# Revit family: Solarstone - Solarpanels
name_source: partatom
category: Generic Models
revit_build: Autodesk Revit 2018 (Build: 20170223_1515(x64)
units: mm (PartAtom-declared; Revit-internal decimal feet)

## family parameters
Always vertical = No
Can host rebar = No
Cut with Voids When Loaded = Yes
OmniClass Number = 23.80.00.00
OmniClass Title = Electric Power and Lighting
Part Type = Normal
Room Calculation Point = No
Round Connector Dimension = Use Diameter
Shared = No
Work Plane-Based = Yes

## types (2) — shared parameters
Aluminium Framing = SolarStone® - Aluminium, Painted
Default Panel Overlap = 43 mm
Developer = TULITEC
Developer URL = http://tulitec.com
Finishing Profile = SolarStone® - Finishing Profile
Fixing Plate = SolarStone® - Fixing Plate
Fuse Rating = 0 A
IFCExportAS = IfcDiscreteAccessoryType
Manufacturer = Solarstone
Manufacturer URL = https://solarstone.ee
Max Panel Vertical Overlap = 130 mm
Max Solar Panel Height = 2400 mm
Max Solar Panel Width = 2400 mm
Maximum Power Current (Imp) = 0 A
Maximum Power Rating (Pmax) = 0 VA
Maximum Power Voltage (Vmp) = 0 V
Maximum System Voltage = 0 V
Min Solar Panel Height = 900 mm
Min Solar Panel Width = 900 mm
Mono Perc Solar Cells = SolarStone® - Mono Perc Solar Cell
Offset = -5 mm  [stored -0.0164042 ft]
Open Circuit Voltage (Voc) = 0 V
Panel Thickness = 39 mm
Panels Vertical Spacing = 25 mm  [stored 0.082021 ft]
Power Temperature Coefficient = 0%/°C
Short Circuit Current (Isc) = 0 A
Static Load Test Passed = 0.00 kg/m²
Tolerance of Maximum Power Rating = 0%
Top Profile Dimension = 161 mm  [stored 0.528215 ft]
zero-valued in all types: Default Elevation, Min Panel Vertical Overlap, Module Efficiency (%), Number of cells, Weight (kg)

## per-type parameters (varying)
| type | Cell Visibility |
| Solarstone - Solarpanels | Yes |
| Solarstone - Blind Panel | No |

note: [stored X ft] marks values corroborated as IEEE doubles in the binary element streams (Revit-internal decimal feet)

## geometry (parser evidence)
native form markers: Sweep x20
no freeform markers — native parametric forms only
